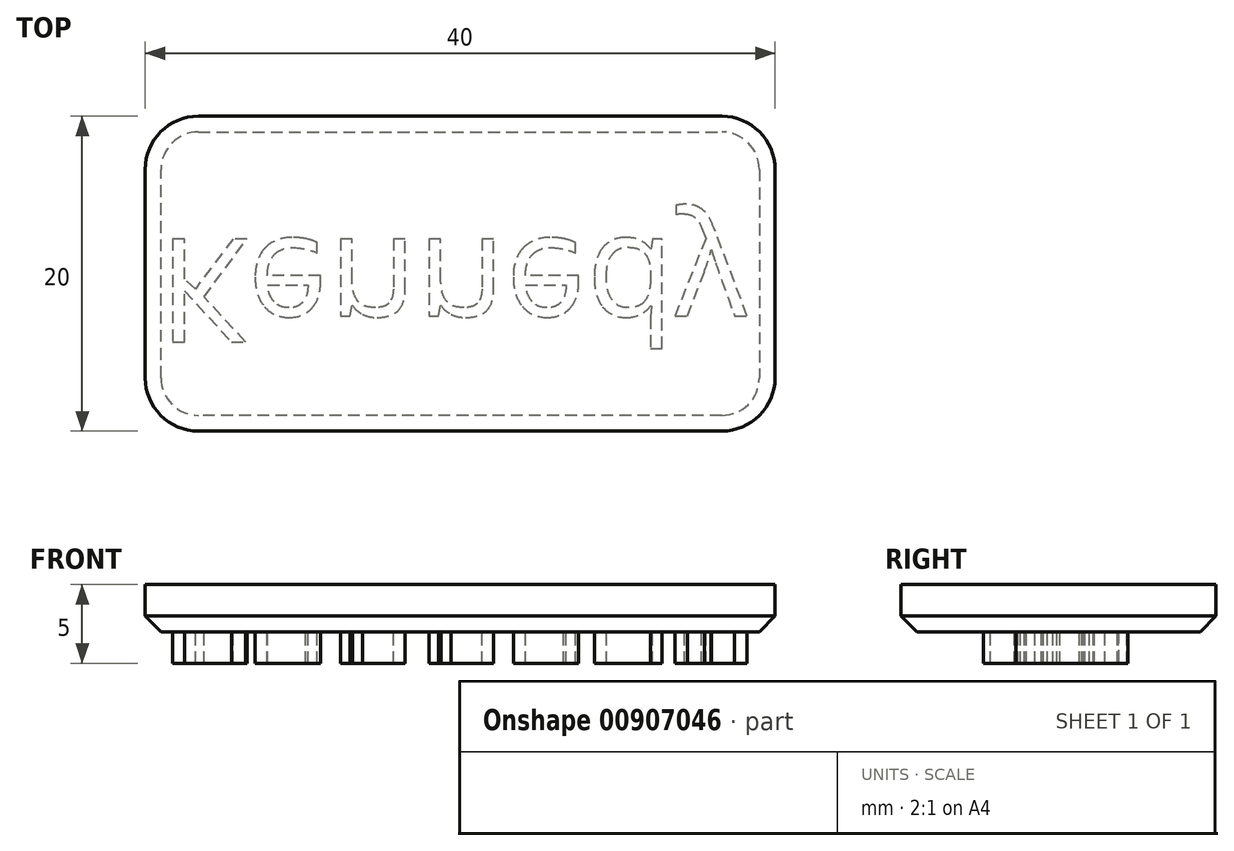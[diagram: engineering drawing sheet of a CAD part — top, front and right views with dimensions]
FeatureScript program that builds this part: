
annotation { "Feature Type Name" : "Feature", "Feature Type Description" : "" }
export const myFeature = defineFeature(function(context is Context, id is Id, definition is map)
    precondition{}
    {
        {
            var Q0;
            Q0=qCreatedBy(makeId("Top.planeOp"),FACE);
            var sketch = newSketch(context, id + "F0", { "sketchPlane" : qUnion([Q0])});
            skLineSegment(sketch, "E0.bottom", {"start": v(0, 0) * mm, "end": v(-40, 0) * mm});
            skLineSegment(sketch, "E0.top", {"start": v(0, 20) * mm, "end": v(-40, 20) * mm});
            skLineSegment(sketch, "E0.left", {"start": v(0, 0) * mm, "end": v(0, 20) * mm});
            skLineSegment(sketch, "E0.right", {"start": v(-40, 0) * mm, "end": v(-40, 20) * mm});
            skSolve(sketch);
        }
        {
            var Q0;
            Q0 = qSketchRegion(id + "F0", true);
            extrude(context, id + "F1", {"entities" : qUnion([Q0]), "depth" : 3 * mm, "offsetDistance" : 25 * mm});
        }
        {
            var Q0;
            Q0=makeQuery(id+"F1.opExtrude","CAP_FACE",FACE,{"disambiguationData":[OSD([sQuery(id+"F0.wireOp",EDGE,"E0.bottom"),sQuery(id+"F0.wireOp",EDGE,"E0.top"),sQuery(id+"F0.wireOp",EDGE,"E0.left"),sQuery(id+"F0.wireOp",EDGE,"E0.right")])],"isStart":true});
            var sketch = newSketch(context, id + "F2", { "sketchPlane" : qUnion([Q0])});
            skText(sketch, "E1", { "text": "Kennedy ", "fontName": "OpenSans-Regular.ttf"});
            const initialGuessF2  = {"E1": [-0.03916, -0.01221, 1, 0, 0.0066]};
            skSetInitialGuess(sketch, initialGuessF2);
            skSolve(sketch);
        }
        {
            var Q0;
            Q0=makeQuery(id+"F2.imprint","IMPRINT",FACE,{"disambiguationData":[TD([[makeQuery(id+"F2.imprint","IMPRINT",EDGE,{"derivedFrom":sQuery(id+"F2.wireOp",EDGE,"E1.sketch_text.stroke-0")}),-1.0]])]});
            var Q1;
            Q1=makeQuery(id+"F2.imprint","IMPRINT",FACE,{"disambiguationData":[TD([[makeQuery(id+"F2.imprint","IMPRINT",EDGE,{"derivedFrom":sQuery(id+"F2.wireOp",EDGE,"E1.sketch_text.stroke-12")}),-1.0]])]});
            var Q2;
            Q2=makeQuery(id+"F2.imprint","IMPRINT",FACE,{"disambiguationData":[TD([[makeQuery(id+"F2.imprint","IMPRINT",EDGE,{"derivedFrom":sQuery(id+"F2.wireOp",EDGE,"E1.sketch_text.stroke-31")}),-1.0]])]});
            var Q3;
            Q3=makeQuery(id+"F2.imprint","IMPRINT",FACE,{"disambiguationData":[TD([[makeQuery(id+"F2.imprint","IMPRINT",EDGE,{"derivedFrom":sQuery(id+"F2.wireOp",EDGE,"E1.sketch_text.stroke-48")}),-1.0]])]});
            var Q4;
            Q4=makeQuery(id+"F2.imprint","IMPRINT",FACE,{"disambiguationData":[TD([[makeQuery(id+"F2.imprint","IMPRINT",EDGE,{"derivedFrom":sQuery(id+"F2.wireOp",EDGE,"E1.sketch_text.stroke-65")}),-1.0]])]});
            var Q5;
            Q5=makeQuery(id+"F2.imprint","IMPRINT",FACE,{"disambiguationData":[TD([[makeQuery(id+"F2.imprint","IMPRINT",EDGE,{"derivedFrom":sQuery(id+"F2.wireOp",EDGE,"E1.sketch_text.stroke-84")}),-1.0]])]});
            var Q6;
            Q6=makeQuery(id+"F2.imprint","IMPRINT",FACE,{"disambiguationData":[TD([[makeQuery(id+"F2.imprint","IMPRINT",EDGE,{"derivedFrom":sQuery(id+"F2.wireOp",EDGE,"E1.sketch_text.stroke-108")}),-1.0]])]});
            extrude(context, id + "F3", {"entities" : qUnion([Q0, Q1, Q2, Q3, Q4, Q5, Q6]), "operationType" : NewBodyOperationType.ADD, "depth" : 2 * mm, "offsetDistance" : 25 * mm});
        }
        {
            var Q0;
            Q0=makeQuery(id+"F1.opExtrude","SWEPT_EDGE",EDGE,{"disambiguationData":[OSD([sQuery(id+"F0.wireOp",EDGE,"E0.top"),sQuery(id+"F0.wireOp",EDGE,"E0.left")])]});
            var Q1;
            Q1=makeQuery(id+"F1.opExtrude","SWEPT_EDGE",EDGE,{"disambiguationData":[OSD([sQuery(id+"F0.wireOp",EDGE,"E0.bottom"),sQuery(id+"F0.wireOp",EDGE,"E0.left")])]});
            var Q2;
            Q2=makeQuery(id+"F1.opExtrude","SWEPT_EDGE",EDGE,{"disambiguationData":[OSD([sQuery(id+"F0.wireOp",EDGE,"E0.bottom"),sQuery(id+"F0.wireOp",EDGE,"E0.right")])]});
            var Q3;
            Q3=makeQuery(id+"F1.opExtrude","SWEPT_EDGE",EDGE,{"disambiguationData":[OSD([sQuery(id+"F0.wireOp",EDGE,"E0.top"),sQuery(id+"F0.wireOp",EDGE,"E0.right")])]});
            fillet(context, id + "F4", {"entities" : qUnion([Q0, Q1, Q2, Q3]), "radius" : 3.38 * mm, "tangentPropagation" : true, "allowEdgeOverflow" : false});
        }
        {
            var Q0;
            Q0=makeQuery(id+"F1.opExtrude","CAP_EDGE",EDGE,{"disambiguationData":[OSD([sQuery(id+"F0.wireOp",EDGE,"E0.right")])],"isStart":true});
            var Q1;
            {var subQ0=sQuery(id+"F0.wireOp",EDGE,"E0.top");var subQ1=sQuery(id+"F0.wireOp",EDGE,"E0.right");var subQ2=sQuery(id+"F0.wireOp",EDGE,"E0.bottom");var subQ3=sQuery(id+"F0.wireOp",EDGE,"E0.left");Q1=makeQuery(id+"F4.opFillet","BLEND_EDGE",EDGE,{"blendedFrom":[makeQuery(id+"F1.opExtrude","SWEPT_EDGE",EDGE,{"disambiguationData":[OSD([subQ2,subQ1])]}),makeQuery(id+"F3.boolean.opBoolean","SPLIT",FACE,{"disambiguationData":[TD([makeQuery(id+"F1.opExtrude","SWEPT_FACE",FACE,{"disambiguationData":[OSD([subQ2])]})])],"derivedFrom":makeQuery(id+"F1.opExtrude","CAP_FACE",FACE,{"disambiguationData":[OSD([subQ2,subQ0,subQ3,subQ1])],"isStart":true})})],"blendedInto":[makeQuery(id+"F3.boolean.opBoolean","SPLIT",FACE,{"disambiguationData":[TD([makeQuery(id+"F1.opExtrude","SWEPT_FACE",FACE,{"disambiguationData":[OSD([subQ2])]})])],"derivedFrom":makeQuery(id+"F1.opExtrude","CAP_FACE",FACE,{"disambiguationData":[OSD([subQ2,subQ0,subQ3,subQ1])],"isStart":true})})]});}
            var Q2;
            Q2=makeQuery(id+"F1.opExtrude","CAP_EDGE",EDGE,{"disambiguationData":[OSD([sQuery(id+"F0.wireOp",EDGE,"E0.bottom")])],"isStart":true});
            var Q3;
            {var subQ0=sQuery(id+"F0.wireOp",EDGE,"E0.top");var subQ1=sQuery(id+"F0.wireOp",EDGE,"E0.right");var subQ2=sQuery(id+"F0.wireOp",EDGE,"E0.bottom");var subQ3=sQuery(id+"F0.wireOp",EDGE,"E0.left");Q3=makeQuery(id+"F4.opFillet","BLEND_EDGE",EDGE,{"blendedFrom":[makeQuery(id+"F1.opExtrude","SWEPT_EDGE",EDGE,{"disambiguationData":[OSD([subQ0,subQ1])]}),makeQuery(id+"F3.boolean.opBoolean","SPLIT",FACE,{"disambiguationData":[TD([makeQuery(id+"F1.opExtrude","SWEPT_FACE",FACE,{"disambiguationData":[OSD([subQ2])]})])],"derivedFrom":makeQuery(id+"F1.opExtrude","CAP_FACE",FACE,{"disambiguationData":[OSD([subQ2,subQ0,subQ3,subQ1])],"isStart":true})})],"blendedInto":[makeQuery(id+"F3.boolean.opBoolean","SPLIT",FACE,{"disambiguationData":[TD([makeQuery(id+"F1.opExtrude","SWEPT_FACE",FACE,{"disambiguationData":[OSD([subQ2])]})])],"derivedFrom":makeQuery(id+"F1.opExtrude","CAP_FACE",FACE,{"disambiguationData":[OSD([subQ2,subQ0,subQ3,subQ1])],"isStart":true})})]});}
            var Q4;
            Q4=makeQuery(id+"F1.opExtrude","CAP_EDGE",EDGE,{"disambiguationData":[OSD([sQuery(id+"F0.wireOp",EDGE,"E0.top")])],"isStart":true});
            var Q5;
            {var subQ0=sQuery(id+"F0.wireOp",EDGE,"E0.top");var subQ1=sQuery(id+"F0.wireOp",EDGE,"E0.right");var subQ2=sQuery(id+"F0.wireOp",EDGE,"E0.bottom");var subQ3=sQuery(id+"F0.wireOp",EDGE,"E0.left");Q5=makeQuery(id+"F4.opFillet","BLEND_EDGE",EDGE,{"blendedFrom":[makeQuery(id+"F1.opExtrude","SWEPT_EDGE",EDGE,{"disambiguationData":[OSD([subQ0,subQ3])]}),makeQuery(id+"F3.boolean.opBoolean","SPLIT",FACE,{"disambiguationData":[TD([makeQuery(id+"F1.opExtrude","SWEPT_FACE",FACE,{"disambiguationData":[OSD([subQ2])]})])],"derivedFrom":makeQuery(id+"F1.opExtrude","CAP_FACE",FACE,{"disambiguationData":[OSD([subQ2,subQ0,subQ3,subQ1])],"isStart":true})})],"blendedInto":[makeQuery(id+"F3.boolean.opBoolean","SPLIT",FACE,{"disambiguationData":[TD([makeQuery(id+"F1.opExtrude","SWEPT_FACE",FACE,{"disambiguationData":[OSD([subQ2])]})])],"derivedFrom":makeQuery(id+"F1.opExtrude","CAP_FACE",FACE,{"disambiguationData":[OSD([subQ2,subQ0,subQ3,subQ1])],"isStart":true})})]});}
            var Q6;
            Q6=makeQuery(id+"F1.opExtrude","CAP_EDGE",EDGE,{"disambiguationData":[OSD([sQuery(id+"F0.wireOp",EDGE,"E0.left")])],"isStart":true});
            var Q7;
            {var subQ0=sQuery(id+"F0.wireOp",EDGE,"E0.top");var subQ1=sQuery(id+"F0.wireOp",EDGE,"E0.right");var subQ2=sQuery(id+"F0.wireOp",EDGE,"E0.bottom");var subQ3=sQuery(id+"F0.wireOp",EDGE,"E0.left");Q7=makeQuery(id+"F4.opFillet","BLEND_EDGE",EDGE,{"blendedFrom":[makeQuery(id+"F1.opExtrude","SWEPT_EDGE",EDGE,{"disambiguationData":[OSD([subQ2,subQ3])]}),makeQuery(id+"F3.boolean.opBoolean","SPLIT",FACE,{"disambiguationData":[TD([makeQuery(id+"F1.opExtrude","SWEPT_FACE",FACE,{"disambiguationData":[OSD([subQ2])]})])],"derivedFrom":makeQuery(id+"F1.opExtrude","CAP_FACE",FACE,{"disambiguationData":[OSD([subQ2,subQ0,subQ3,subQ1])],"isStart":true})})],"blendedInto":[makeQuery(id+"F3.boolean.opBoolean","SPLIT",FACE,{"disambiguationData":[TD([makeQuery(id+"F1.opExtrude","SWEPT_FACE",FACE,{"disambiguationData":[OSD([subQ2])]})])],"derivedFrom":makeQuery(id+"F1.opExtrude","CAP_FACE",FACE,{"disambiguationData":[OSD([subQ2,subQ0,subQ3,subQ1])],"isStart":true})})]});}
            chamfer(context, id + "F5", {"entities" : qUnion([Q0, Q1, Q2, Q3, Q4, Q5, Q6, Q7]), "width" : 1 * mm, "tangentPropagation" : true});
        }
    });
